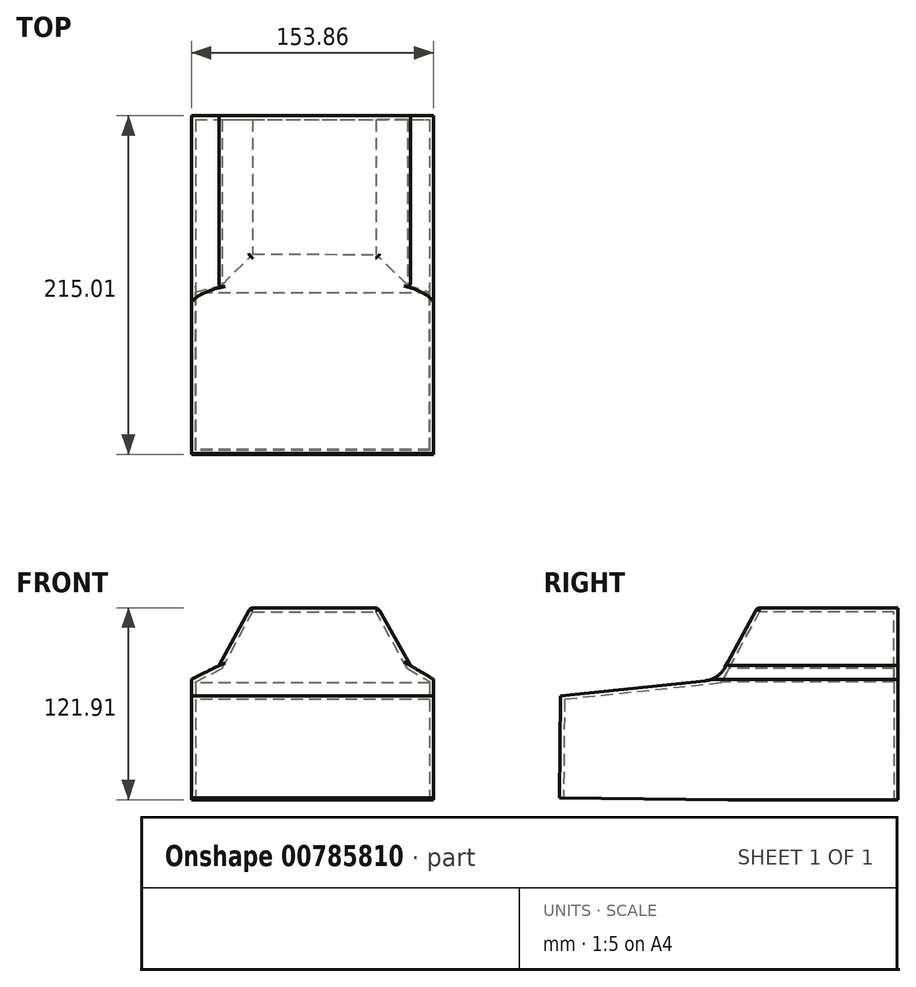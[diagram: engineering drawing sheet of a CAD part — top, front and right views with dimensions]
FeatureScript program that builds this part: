
annotation { "Feature Type Name" : "Feature", "Feature Type Description" : "" }
export const myFeature = defineFeature(function(context is Context, id is Id, definition is map)
    precondition{}
    {
        {
            var Q0;
            Q0=qCreatedBy(makeId("Front.planeOp"),FACE);
            var sketch = newSketch(context, id + "F0", { "sketchPlane" : qUnion([Q0])});
            skLineSegment(sketch, "E0.top", {"start": v(-77.01, -76.44) * mm, "end": v(76.85, -76.44) * mm});
            skLineSegment(sketch, "E0.left", {"start": v(-77.01, 0) * mm, "end": v(-77.01, -76.44) * mm});
            skLineSegment(sketch, "E0.right", {"start": v(76.85, 0) * mm, "end": v(76.85, -76.44) * mm});
            skLineSegment(sketch, "E1", {"start": v(-77.01, 0) * mm, "end": v(-59.47, 8.73) * mm});
            skLineSegment(sketch, "E2", {"start": v(62.1, 8.73) * mm, "end": v(76.85, 0) * mm});
            skLineSegment(sketch, "E3", {"start": v(-59.47, 8.73) * mm, "end": v(-39.52, 45.47) * mm});
            skLineSegment(sketch, "E4", {"start": v(-39.52, 45.47) * mm, "end": v(41.62, 45.37) * mm});
            skLineSegment(sketch, "E5", {"start": v(62.1, 8.73) * mm, "end": v(41.62, 45.37) * mm});
            skSolve(sketch);
        }
        {
            var Q0;
            Q0 = qSketchRegion(id + "F0", true);
            extrude(context, id + "F1", {"entities" : qUnion([Q0]), "oppositeDirection" : true, "depth" : 89.13 * mm, "offsetDistance" : 25.4 * mm});
        }
        {
            var Q0;
            Q0=qCreatedBy(makeId("Right.planeOp"),FACE);
            var sketch = newSketch(context, id + "F2", { "sketchPlane" : qUnion([Q0])});
            skLineSegment(sketch, "E6", {"start": v(0, 46.09) * mm, "end": v(-24.94, 0) * mm});
            skLineSegment(sketch, "E7", {"start": v(-24.94, 0) * mm, "end": v(-125.25, -10.54) * mm});
            skLineSegment(sketch, "E8", {"start": v(-125.25, -10.54) * mm, "end": v(-125.88, -75.4) * mm});
            skLineSegment(sketch, "E9", {"start": v(-125.88, -75.4) * mm, "end": v(0, -76.62) * mm});
            skLineSegment(sketch, "E10", {"start": v(0, 46.09) * mm, "end": v(0, -76.62) * mm});
            skSolve(sketch);
        }
        {
            var Q0;
            Q0 = qSketchRegion(id + "F2", true);
            extrude(context, id + "F3", {"entities" : qUnion([Q0]), "operationType" : NewBodyOperationType.ADD, "endBound" : BoundingType.SYMMETRIC, "depth" : 154.28 * mm, "offsetDistance" : 25.4 * mm});
        }
        {
            var Q0;
            Q0=makeQuery(id+"F3.opExtrude","SWEPT_FACE",FACE,{"disambiguationData":[OSD([sQuery(id+"F2.wireOp",EDGE,"E10")])]});
            extrude(context, id + "F4", {"entities" : qUnion([Q0]), "operationType" : NewBodyOperationType.REMOVE, "oppositeDirection" : true, "depth" : 218.77 * mm, "offsetDistance" : 25.4 * mm});
        }
        {
            var Q0;
            Q0=makeQuery(id+"F3.opExtrude","SWEPT_FACE",FACE,{"disambiguationData":[OSD([sQuery(id+"F2.wireOp",EDGE,"E9")])]});
            var Q1;
            {var subQ0=sQuery(id+"F0.wireOp",EDGE,"E0.top");Q1=makeQuery(id+"F4.boolean.opBoolean","MERGE",FACE,{"derivedFrom":[makeQuery(id+"F1.opExtrude","SWEPT_FACE",FACE,{"disambiguationData":[OSD([subQ0])]}),makeQuery(id+"F4.opExtrude","SWEPT_FACE",FACE,{"disambiguationData":[OSD([subQ0])]})]});}
            shell(context, id + "F5", {"entities" : qUnion([Q0, Q1]), "thickness" : 2.54 * mm});
        }
        {
            var Q0;
            Q0=makeQuery(id+"F3.opExtrude","SWEPT_EDGE",EDGE,{"disambiguationData":[OSD([sQuery(id+"F2.wireOp",EDGE,"E6"),sQuery(id+"F2.wireOp",EDGE,"E7")])]});
            fillet(context, id + "F6", {"entities" : qUnion([Q0]), "radius" : 15.58 * mm, "tangentPropagation" : true, "allowEdgeOverflow" : false});
        }
        {
            var Q0;
            Q0=makeQuery(id+"F4.boolean.opBoolean","INTERSECT",EDGE,{"derivedFrom":[makeQuery(id+"F3.opExtrude","SWEPT_FACE",FACE,{"disambiguationData":[OSD([sQuery(id+"F2.wireOp",EDGE,"E6")])]}),makeQuery(id+"F4.opExtrude","SWEPT_FACE",FACE,{"disambiguationData":[OSD([sQuery(id+"F0.wireOp",EDGE,"E3")])]})]});
            var Q1;
            Q1=makeQuery(id+"F4.boolean.opBoolean","INTERSECT",EDGE,{"derivedFrom":[makeQuery(id+"F3.opExtrude","SWEPT_FACE",FACE,{"disambiguationData":[OSD([sQuery(id+"F2.wireOp",EDGE,"E6")])]}),makeQuery(id+"F4.opExtrude","SWEPT_FACE",FACE,{"disambiguationData":[OSD([sQuery(id+"F0.wireOp",EDGE,"E5")])]})]});
            var Q2;
            Q2=makeQuery(id+"F4.boolean.opBoolean","INTERSECT",EDGE,{"derivedFrom":[makeQuery(id+"F3.opExtrude","SWEPT_FACE",FACE,{"disambiguationData":[OSD([sQuery(id+"F2.wireOp",EDGE,"E6")])]}),makeQuery(id+"F4.opExtrude","SWEPT_FACE",FACE,{"disambiguationData":[OSD([sQuery(id+"F0.wireOp",EDGE,"E4")])]})]});
            var Q3;
            {var subQ0=sQuery(id+"F0.wireOp",EDGE,"E5");var subQ1=sQuery(id+"F0.wireOp",EDGE,"E4");Q3=makeQuery(id+"F4.boolean.opBoolean","MERGE",EDGE,{"derivedFrom":[makeQuery(id+"F1.opExtrude","SWEPT_EDGE",EDGE,{"disambiguationData":[OSD([subQ1,subQ0])]}),makeQuery(id+"F4.opExtrude","SWEPT_EDGE",EDGE,{"disambiguationData":[OSD([subQ1,subQ0])]})]});}
            var Q4;
            {var subQ0=sQuery(id+"F0.wireOp",EDGE,"E4");var subQ1=sQuery(id+"F0.wireOp",EDGE,"E3");Q4=makeQuery(id+"F4.boolean.opBoolean","MERGE",EDGE,{"derivedFrom":[makeQuery(id+"F1.opExtrude","SWEPT_EDGE",EDGE,{"disambiguationData":[OSD([subQ1,subQ0])]}),makeQuery(id+"F4.opExtrude","SWEPT_EDGE",EDGE,{"disambiguationData":[OSD([subQ1,subQ0])]})]});}
            fillet(context, id + "F7", {"entities" : qUnion([Q0, Q1, Q2, Q3, Q4]), "radius" : 3.1 * mm, "tangentPropagation" : true, "allowEdgeOverflow" : false});
        }
    });
